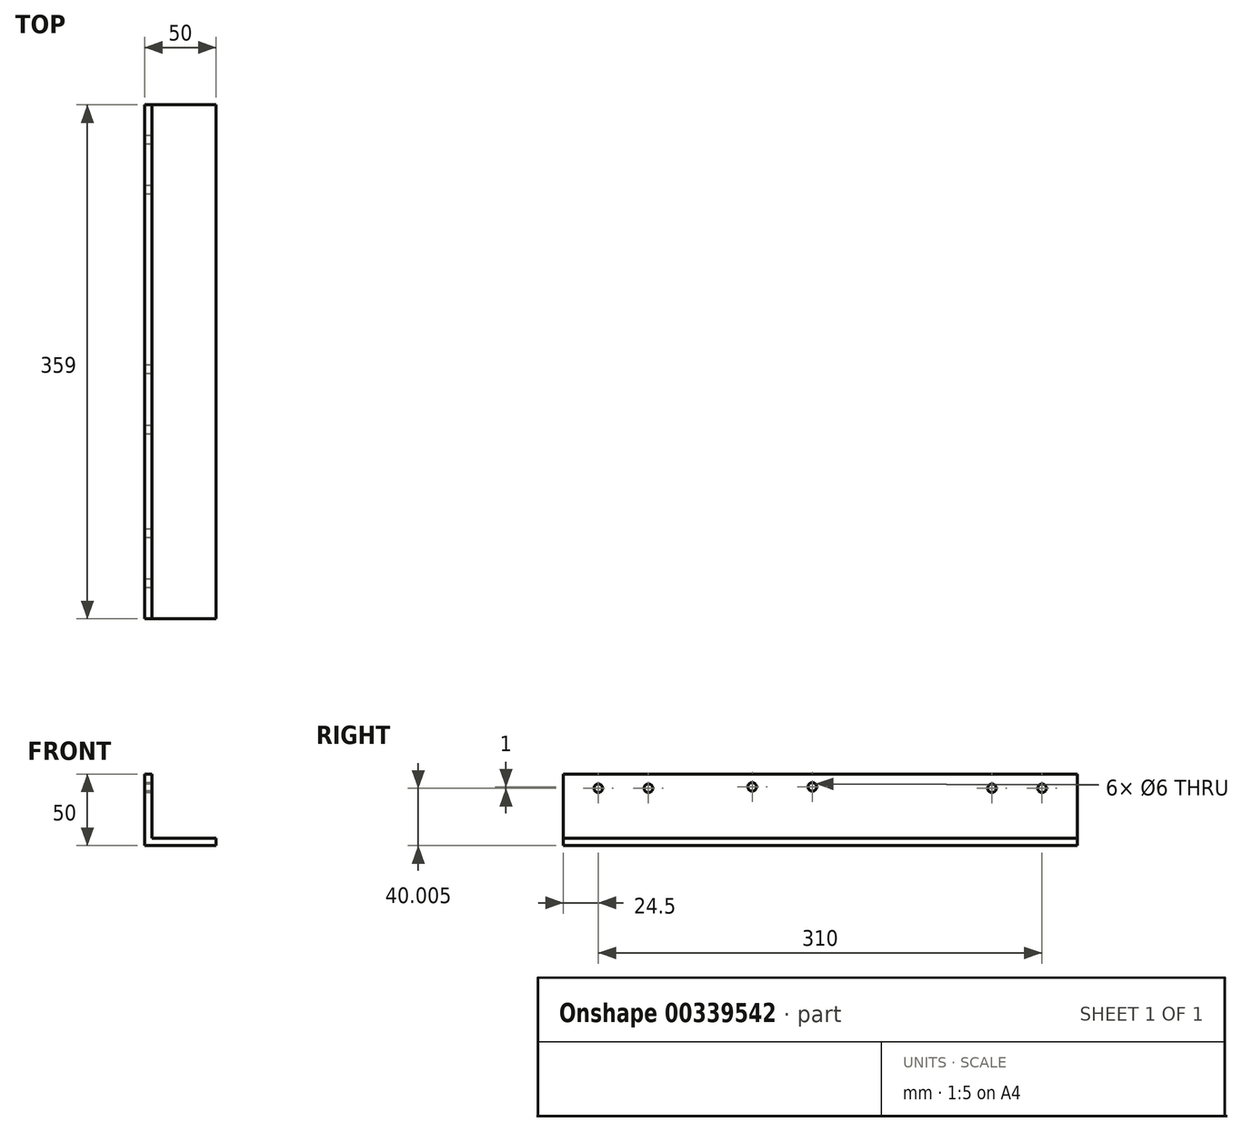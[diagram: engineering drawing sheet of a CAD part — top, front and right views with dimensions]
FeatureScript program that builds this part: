
annotation { "Feature Type Name" : "Feature", "Feature Type Description" : "" }
export const myFeature = defineFeature(function(context is Context, id is Id, definition is map)
    precondition{}
    {
        {
            var Q0;
            Q0=qCreatedBy(makeId("Front.planeOp"),FACE);
            var sketch = newSketch(context, id + "F0", { "sketchPlane" : qUnion([Q0])});
            skLineSegment(sketch, "E0", {"start": v(-21.62, 26.48) * mm, "end": v(-21.62, -23.52) * mm});
            skLineSegment(sketch, "E1", {"start": v(-21.62, -23.52) * mm, "end": v(28.38, -23.52) * mm});
            skLineSegment(sketch, "E2", {"start": v(28.38, -23.52) * mm, "end": v(28.38, -18.52) * mm});
            skLineSegment(sketch, "E3", {"start": v(28.38, -18.52) * mm, "end": v(-16.62, -18.52) * mm});
            skLineSegment(sketch, "E4", {"start": v(-16.62, -18.52) * mm, "end": v(-16.62, 26.48) * mm});
            skLineSegment(sketch, "E5", {"start": v(-16.62, 26.48) * mm, "end": v(-21.62, 26.48) * mm});
            skSolve(sketch);
        }
        {
            var Q0;
            Q0 = qSketchRegion(id + "F0", true);
            extrude(context, id + "F1", {"entities" : qUnion([Q0]), "depth" : 359 * mm});
        }
        {
            var Q0;
            Q0=qCreatedBy(makeId("Right.planeOp"),FACE);
            var sketch = newSketch(context, id + "F2", { "sketchPlane" : qUnion([Q0])});
            skCircle(sketch, "E6", {"center": v(-334.5, 16.48) * mm, "radius": 3 * mm});
            skCircle(sketch, "E7", {"center": v(-24.5, 16.48) * mm, "radius": 3 * mm});
            skCircle(sketch, "E8", {"center": v(-299.5, 16.48) * mm, "radius": 3 * mm});
            skCircle(sketch, "E9", {"center": v(-59.5, 16.48) * mm, "radius": 3 * mm});
            skCircle(sketch, "E10", {"center": v(-185, 17.48) * mm, "radius": 3 * mm});
            skCircle(sketch, "E11", {"center": v(-227, 17.48) * mm, "radius": 3 * mm});
            skSolve(sketch);
        }
        {
            var Q0;
            Q0=sQuery(id+"F2.wireOp",VERTEX,"E6.center");
            var Q1;
            Q1=makeQuery(id+"F1.opExtrude","SWEPT_BODY",BODY,{"disambiguationData":[OSD([sQuery(id+"F0.wireOp",EDGE,"E0"),sQuery(id+"F0.wireOp",EDGE,"E1"),sQuery(id+"F0.wireOp",EDGE,"E2"),sQuery(id+"F0.wireOp",EDGE,"E3"),sQuery(id+"F0.wireOp",EDGE,"E4"),sQuery(id+"F0.wireOp",EDGE,"E5")])]});
            hole(context, id + "F3", {"style" : HoleStyle.SIMPLE, "endStyle" : HoleEndStyle.THROUGH, "holeDiameter" : 6 * mm, "isTappedThrough" : true, "tappedDepth" : 12 * mm, "tapClearance" : 3, "startFromSketch" : true, "locations" : qUnion([Q0]), "scope" : qUnion([Q1])});
        }
        {
            var Q0;
            Q0=sQuery(id+"F2.wireOp",VERTEX,"E7.center");
            var Q1;
            Q1=makeQuery(id+"F1.opExtrude","SWEPT_BODY",BODY,{"disambiguationData":[OSD([sQuery(id+"F0.wireOp",EDGE,"E0"),sQuery(id+"F0.wireOp",EDGE,"E1"),sQuery(id+"F0.wireOp",EDGE,"E2"),sQuery(id+"F0.wireOp",EDGE,"E3"),sQuery(id+"F0.wireOp",EDGE,"E4"),sQuery(id+"F0.wireOp",EDGE,"E5")])]});
            hole(context, id + "F4", {"style" : HoleStyle.SIMPLE, "endStyle" : HoleEndStyle.THROUGH, "holeDiameter" : 6 * mm, "isTappedThrough" : true, "tappedDepth" : 12 * mm, "tapClearance" : 3, "startFromSketch" : true, "locations" : qUnion([Q0]), "scope" : qUnion([Q1])});
        }
        {
            var Q0;
            Q0=sQuery(id+"F2.wireOp",VERTEX,"E8.center");
            var Q1;
            Q1=makeQuery(id+"F1.opExtrude","SWEPT_BODY",BODY,{"disambiguationData":[OSD([sQuery(id+"F0.wireOp",EDGE,"E0"),sQuery(id+"F0.wireOp",EDGE,"E1"),sQuery(id+"F0.wireOp",EDGE,"E2"),sQuery(id+"F0.wireOp",EDGE,"E3"),sQuery(id+"F0.wireOp",EDGE,"E4"),sQuery(id+"F0.wireOp",EDGE,"E5")])]});
            hole(context, id + "F5", {"style" : HoleStyle.SIMPLE, "endStyle" : HoleEndStyle.THROUGH, "holeDiameter" : 6 * mm, "isTappedThrough" : true, "tappedDepth" : 12 * mm, "tapClearance" : 3, "startFromSketch" : true, "locations" : qUnion([Q0]), "scope" : qUnion([Q1])});
        }
        {
            var Q0;
            Q0=sQuery(id+"F2.wireOp",VERTEX,"E9.center");
            var Q1;
            Q1=makeQuery(id+"F1.opExtrude","SWEPT_BODY",BODY,{"disambiguationData":[OSD([sQuery(id+"F0.wireOp",EDGE,"E0"),sQuery(id+"F0.wireOp",EDGE,"E1"),sQuery(id+"F0.wireOp",EDGE,"E2"),sQuery(id+"F0.wireOp",EDGE,"E3"),sQuery(id+"F0.wireOp",EDGE,"E4"),sQuery(id+"F0.wireOp",EDGE,"E5")])]});
            hole(context, id + "F6", {"style" : HoleStyle.SIMPLE, "endStyle" : HoleEndStyle.THROUGH, "holeDiameter" : 6 * mm, "isTappedThrough" : true, "tappedDepth" : 12 * mm, "tapClearance" : 3, "startFromSketch" : true, "locations" : qUnion([Q0]), "scope" : qUnion([Q1])});
        }
        {
            var Q0;
            Q0=sQuery(id+"F2.wireOp",VERTEX,"E11.center");
            var Q1;
            Q1=sQuery(id+"F2.wireOp",VERTEX,"E10.center");
            var Q2;
            Q2=makeQuery(id+"F1.opExtrude","SWEPT_BODY",BODY,{"disambiguationData":[OSD([sQuery(id+"F0.wireOp",EDGE,"E0"),sQuery(id+"F0.wireOp",EDGE,"E1"),sQuery(id+"F0.wireOp",EDGE,"E2"),sQuery(id+"F0.wireOp",EDGE,"E3"),sQuery(id+"F0.wireOp",EDGE,"E4"),sQuery(id+"F0.wireOp",EDGE,"E5")])]});
            hole(context, id + "F7", {"style" : HoleStyle.SIMPLE, "endStyle" : HoleEndStyle.BLIND, "holeDiameter" : 6 * mm, "holeDepth" : 50 * mm, "isTappedThrough" : true, "tappedDepth" : 12 * mm, "tapClearance" : 3, "locations" : qUnion([Q0, Q1]), "scope" : qUnion([Q2])});
        }
    });
